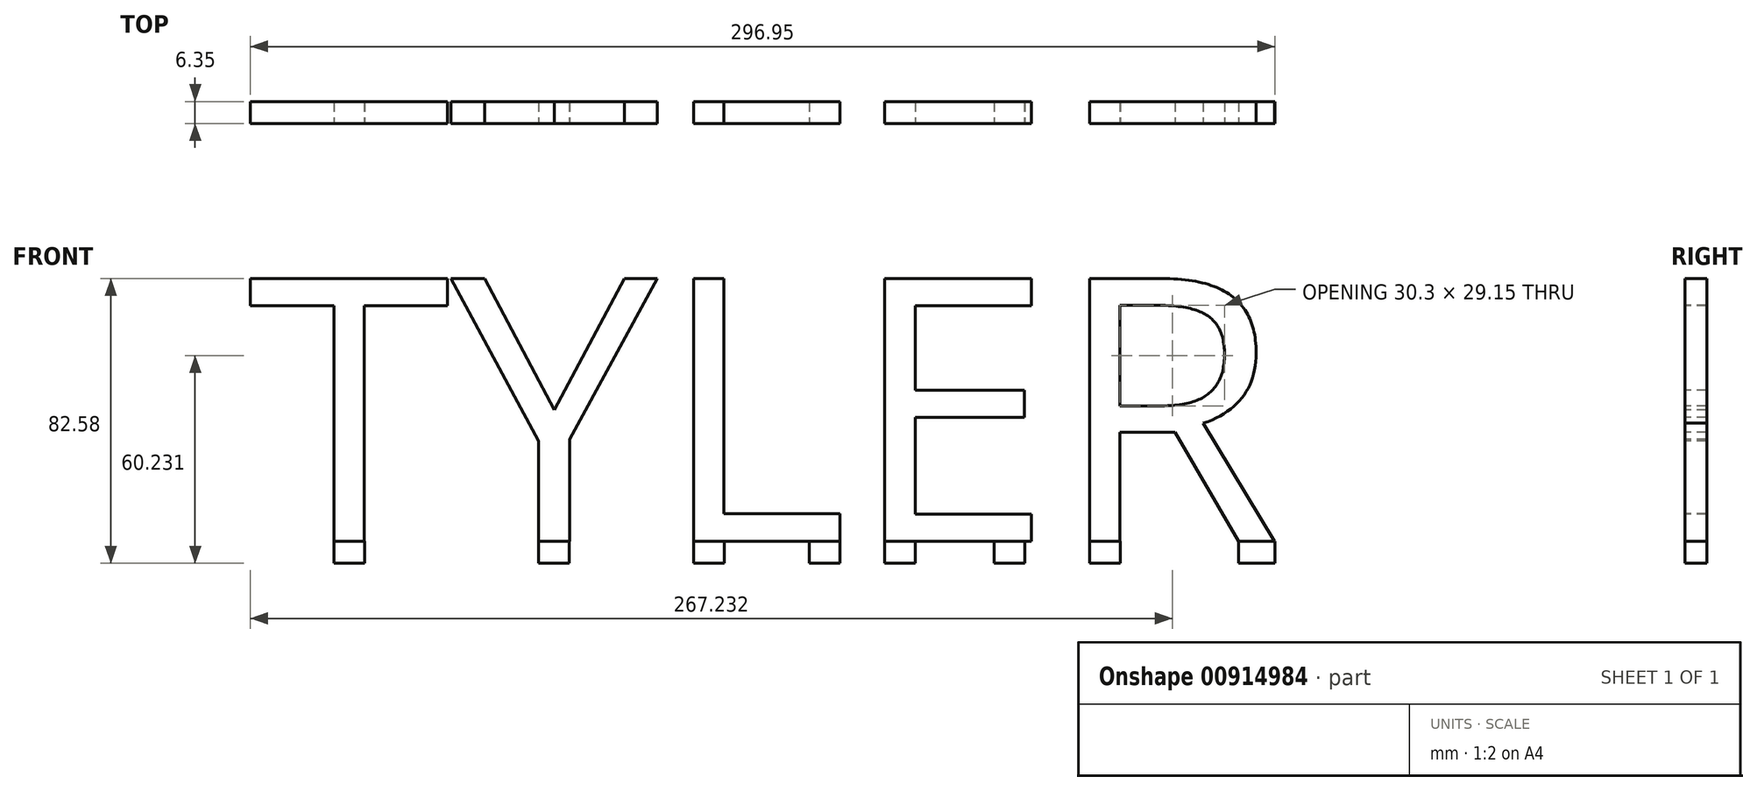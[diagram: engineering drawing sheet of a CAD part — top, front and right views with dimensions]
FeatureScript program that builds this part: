
annotation { "Feature Type Name" : "Feature", "Feature Type Description" : "" }
export const myFeature = defineFeature(function(context is Context, id is Id, definition is map)
    precondition{}
    {
        {
            var Q0;
            Q0=qCreatedBy(makeId("Front.planeOp"),FACE);
            var sketch = newSketch(context, id + "F0", { "sketchPlane" : qUnion([Q0])});
            skText(sketch, "E0", { "text": "TYLER", "fontName": "OpenSans-Regular.ttf"});
            skLineSegment(sketch, "E1", {"start": v(-42.13, 7.08) * mm, "end": v(-42.13, 6.1) * mm});
            skLineSegment(sketch, "E2", {"start": v(-33.17, 7.08) * mm, "end": v(-33.17, 6.98) * mm});
            skLineSegment(sketch, "E3", {"start": v(-92.67, 5.49) * mm, "end": v(-92.67, -9.25) * mm});
            skLineSegment(sketch, "E4", {"start": v(-42.13, -9.25) * mm, "end": v(-42.13, -9.14) * mm});
            skLineSegment(sketch, "E5", {"start": v(2.76, -10.45) * mm, "end": v(2.76, -16.7) * mm});
            skLineSegment(sketch, "E6", {"start": v(45.27, -16.7) * mm, "end": v(45.27, -15.4) * mm});
            skLineSegment(sketch, "E7", {"start": v(160.8, -18.35) * mm, "end": v(171.26, -18.35) * mm});
            skLineSegment(sketch, "E8", {"start": v(126.42, -18.35) * mm, "end": v(160.8, -18.35) * mm});
            skLineSegment(sketch, "E9.bottom", {"start": v(-101.45, -18.35) * mm, "end": v(-92.86, -18.35) * mm});
            skLineSegment(sketch, "E9.top", {"start": v(-101.45, -18.35) * mm, "end": v(-92.86, -18.35) * mm});
            skLineSegment(sketch, "E9.left", {"start": v(-101.45, -18.35) * mm, "end": v(-101.45, -18.35) * mm});
            skLineSegment(sketch, "E9.right", {"start": v(-92.86, -18.35) * mm, "end": v(-92.86, -18.35) * mm});
            skLineSegment(sketch, "E10.bottom", {"start": v(-101.45, -18.35) * mm, "end": v(-92.56, -18.35) * mm});
            skLineSegment(sketch, "E10.top", {"start": v(-101.45, -24.7) * mm, "end": v(-92.56, -24.7) * mm});
            skLineSegment(sketch, "E10.left", {"start": v(-101.45, -18.35) * mm, "end": v(-101.45, -24.7) * mm});
            skLineSegment(sketch, "E10.right", {"start": v(-92.56, -18.35) * mm, "end": v(-92.56, -24.7) * mm});
            skLineSegment(sketch, "E11.bottom", {"start": v(-41.87, -18.35) * mm, "end": v(-33.28, -18.35) * mm});
            skLineSegment(sketch, "E11.top", {"start": v(-41.87, -18.35) * mm, "end": v(-33.28, -18.35) * mm});
            skLineSegment(sketch, "E11.left", {"start": v(-41.87, -18.35) * mm, "end": v(-41.87, -18.35) * mm});
            skLineSegment(sketch, "E11.right", {"start": v(-33.28, -18.35) * mm, "end": v(-33.28, -18.35) * mm});
            skLineSegment(sketch, "E12.bottom", {"start": v(-42.12, -18.35) * mm, "end": v(-33.23, -18.35) * mm});
            skLineSegment(sketch, "E12.top", {"start": v(-42.12, -24.7) * mm, "end": v(-33.23, -24.7) * mm});
            skLineSegment(sketch, "E12.left", {"start": v(-42.12, -18.35) * mm, "end": v(-42.12, -24.7) * mm});
            skLineSegment(sketch, "E12.right", {"start": v(-33.23, -18.35) * mm, "end": v(-33.23, -24.7) * mm});
            skLineSegment(sketch, "E13.bottom", {"start": v(2.78, -18.35) * mm, "end": v(11.67, -18.35) * mm});
            skLineSegment(sketch, "E13.top", {"start": v(2.78, -24.7) * mm, "end": v(11.67, -24.7) * mm});
            skLineSegment(sketch, "E13.left", {"start": v(2.78, -18.35) * mm, "end": v(2.78, -24.7) * mm});
            skLineSegment(sketch, "E13.right", {"start": v(11.67, -18.35) * mm, "end": v(11.67, -24.7) * mm});
            skLineSegment(sketch, "E14.bottom", {"start": v(51.48, -18.35) * mm, "end": v(42.59, -18.35) * mm});
            skLineSegment(sketch, "E15.bottom", {"start": v(36.37, -18.35) * mm, "end": v(45.26, -18.35) * mm});
            skLineSegment(sketch, "E15.top", {"start": v(36.37, -24.7) * mm, "end": v(45.26, -24.7) * mm});
            skLineSegment(sketch, "E15.left", {"start": v(36.37, -18.35) * mm, "end": v(36.37, -24.7) * mm});
            skLineSegment(sketch, "E15.right", {"start": v(45.26, -18.35) * mm, "end": v(45.26, -24.7) * mm});
            skLineSegment(sketch, "E16.bottom", {"start": v(58.17, -18.35) * mm, "end": v(70.06, -18.35) * mm});
            skLineSegment(sketch, "E17.bottom", {"start": v(58.17, -18.35) * mm, "end": v(67.06, -18.35) * mm});
            skLineSegment(sketch, "E17.top", {"start": v(58.17, -24.7) * mm, "end": v(67.06, -24.7) * mm});
            skLineSegment(sketch, "E17.left", {"start": v(58.17, -18.35) * mm, "end": v(58.17, -24.7) * mm});
            skLineSegment(sketch, "E17.right", {"start": v(67.06, -18.35) * mm, "end": v(67.06, -24.7) * mm});
            skLineSegment(sketch, "E18.bottom", {"start": v(89.94, -18.35) * mm, "end": v(98.83, -18.35) * mm});
            skLineSegment(sketch, "E18.top", {"start": v(89.94, -24.7) * mm, "end": v(98.83, -24.7) * mm});
            skLineSegment(sketch, "E18.left", {"start": v(89.94, -18.35) * mm, "end": v(89.94, -24.7) * mm});
            skLineSegment(sketch, "E18.right", {"start": v(98.83, -18.35) * mm, "end": v(98.83, -24.7) * mm});
            skLineSegment(sketch, "E19.bottom", {"start": v(117.57, -18.35) * mm, "end": v(126.46, -18.35) * mm});
            skLineSegment(sketch, "E19.top", {"start": v(117.57, -24.7) * mm, "end": v(126.46, -24.7) * mm});
            skLineSegment(sketch, "E19.left", {"start": v(117.57, -18.35) * mm, "end": v(117.57, -24.7) * mm});
            skLineSegment(sketch, "E19.right", {"start": v(126.46, -18.35) * mm, "end": v(126.46, -24.7) * mm});
            skLineSegment(sketch, "E20.left", {"start": v(160.8, -18.35) * mm, "end": v(160.8, -18.35) * mm});
            skLineSegment(sketch, "E20.right", {"start": v(171.26, -18.35) * mm, "end": v(171.26, -18.35) * mm});
            skLineSegment(sketch, "E21.bottom", {"start": v(160.8, -18.35) * mm, "end": v(171.28, -18.35) * mm});
            skLineSegment(sketch, "E21.top", {"start": v(160.8, -24.7) * mm, "end": v(171.28, -24.7) * mm});
            skLineSegment(sketch, "E21.left", {"start": v(160.8, -18.35) * mm, "end": v(160.8, -24.7) * mm});
            skLineSegment(sketch, "E21.right", {"start": v(171.28, -18.35) * mm, "end": v(171.28, -24.7) * mm});
            const initialGuessF0  = {"E0": [-0.1266, -0.01835, 1, 0, 0.07688]};
            skSetInitialGuess(sketch, initialGuessF0);
            skSolve(sketch);
        }
        {
            var Q0;
            Q0 = qSketchRegion(id + "F0", true);
            extrude(context, id + "F1", {"entities" : qUnion([Q0]), "oppositeDirection" : true, "depth" : 6.35 * mm, "offsetDistance" : 25.4 * mm});
        }
    });
